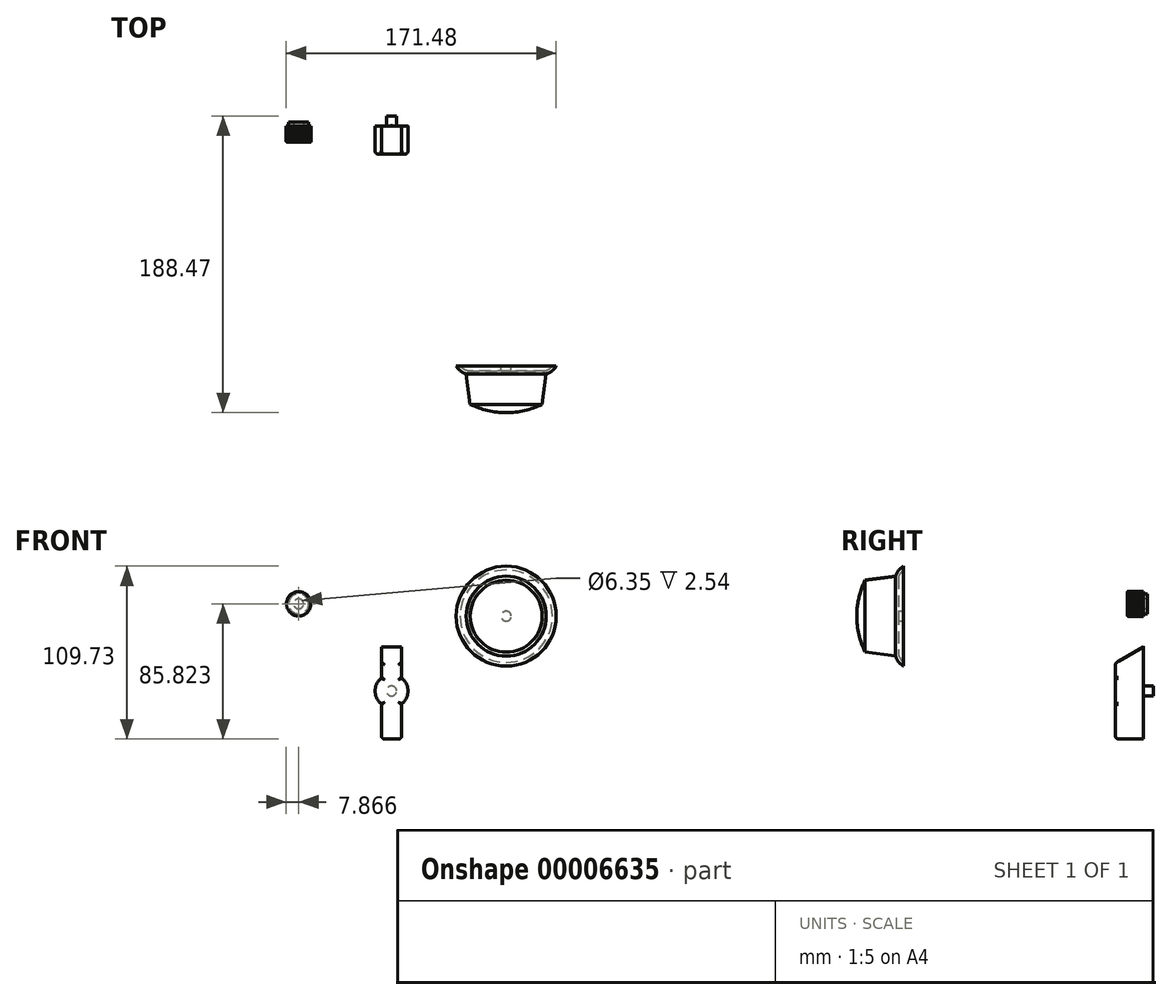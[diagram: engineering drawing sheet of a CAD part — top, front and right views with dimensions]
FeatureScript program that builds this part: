
annotation { "Feature Type Name" : "Feature", "Feature Type Description" : "" }
export const myFeature = defineFeature(function(context is Context, id is Id, definition is map)
    precondition{}
    {
        {
            var Q0;
            Q0=qCreatedBy(makeId("Front.planeOp"),FACE);
            var sketch = newSketch(context, id + "F0", { "sketchPlane" : qUnion([Q0])});
            skArc(sketch, "E0", {"start": v(-6.35, 8.25) * mm, "mid": v(-10.41, 0) * mm, "end": v(-6.35, -8.25) * mm});
            skLineSegment(sketch, "E1", {"start": v(0, 61) * mm, "end": v(0, -89) * mm, "construction": true});
            skLineSegment(sketch, "E2", {"start": v(-6.35, 27.94) * mm, "end": v(-6.35, 8.25) * mm});
            skLineSegment(sketch, "E3", {"start": v(-6.35, -30.48) * mm, "end": v(6.35, -30.48) * mm});
            skLineSegment(sketch, "E4", {"start": v(6.35, -30.48) * mm, "end": v(6.35, -8.25) * mm});
            skLineSegment(sketch, "E5", {"start": v(6.35, 27.94) * mm, "end": v(-6.35, 27.94) * mm});
            skPoint(sketch, "E6", {"position": v(0, 27.94) * mm});
            skLineSegment(sketch, "E7.trimOffspring", {"start": v(6.35, 8.25) * mm, "end": v(6.35, 27.94) * mm});
            skLineSegment(sketch, "E8.trimOffspring", {"start": v(-6.35, -8.25) * mm, "end": v(-6.35, -30.48) * mm});
            skArc(sketch, "E9.trimOffspring", {"start": v(6.35, -8.25) * mm, "mid": v(10.41, 0) * mm, "end": v(6.35, 8.25) * mm});
            skCircle(sketch, "E10", {"center": v(0, 0) * mm, "radius": 3.18 * mm});
            skSolve(sketch);
        }
        {
            var Q0;
            Q0=makeQuery(id+"F0.imprint","IMPRINT",FACE,{"disambiguationData":[TD([[makeQuery(id+"F0.imprint","IMPRINT",EDGE,{"derivedFrom":sQuery(id+"F0.wireOp",EDGE,"E0")}),1.0]])]});
            var Q1;
            Q1=makeQuery(id+"F0.imprint","IMPRINT",FACE,{"disambiguationData":[TD([[makeQuery(id+"F0.imprint","IMPRINT",EDGE,{"derivedFrom":sQuery(id+"F0.wireOp",EDGE,"E10")}),1.0]])]});
            extrude(context, id + "F1", {"entities" : qUnion([Q0, Q1]), "depth" : 17.78 * mm});
        }
        {
            var Q0;
            Q0=makeQuery(id+"F0.imprint","IMPRINT",FACE,{"disambiguationData":[TD([[makeQuery(id+"F0.imprint","IMPRINT",EDGE,{"derivedFrom":sQuery(id+"F0.wireOp",EDGE,"E10")}),1.0]])]});
            var Q1;
            Q1=sQuery(id+"F0.wireOp",EDGE,"E10");
            extrude(context, id + "F2", {"entities" : qUnion([Q0]), "operationType" : NewBodyOperationType.ADD, "surfaceEntities" : qUnion([Q1]), "oppositeDirection" : true, "depth" : 6.35 * mm});
        }
        {
            var Q0;
            Q0=makeQuery(id+"F1.opExtrude","SWEPT_FACE",FACE,{"disambiguationData":[OSD([sQuery(id+"F0.wireOp",EDGE,"E2")])]});
            var sketch = newSketch(context, id + "F3", { "sketchPlane" : qUnion([Q0])});
            skLineSegment(sketch, "E11", {"start": v(-11.17, 0) * mm, "end": v(28.92, 0) * mm, "construction": true});
            skLineSegment(sketch, "E12", {"start": v(0, 27.94) * mm, "end": v(17.78, 17.78) * mm});
            skLineSegment(sketch, "E13", {"start": v(0, 27.94) * mm, "end": v(17.78, 27.94) * mm});
            skLineSegment(sketch, "E14", {"start": v(17.78, 27.94) * mm, "end": v(17.78, 17.78) * mm});
            skSolve(sketch);
        }
        {
            var Q0;
            Q0=makeQuery(id+"F3.imprint","IMPRINT",FACE,{"disambiguationData":[TD([[makeQuery(id+"F3.imprint","IMPRINT",EDGE,{"derivedFrom":sQuery(id+"F3.wireOp",EDGE,"E12")}),1.0]])]});
            extrude(context, id + "F4", {"entities" : qUnion([Q0]), "operationType" : NewBodyOperationType.REMOVE, "oppositeDirection" : true, "depth" : 12.7 * mm});
        }
        {
            var Q0;
            Q0=makeQuery(id+"F4.boolean.opBoolean","COPY",FACE,{"derivedFrom":makeQuery(id+"F4.opExtrude","SWEPT_FACE",FACE,{"disambiguationData":[OSD([sQuery(id+"F3.wireOp",EDGE,"E12")])]})});
            var sketch = newSketch(context, id + "F5", { "sketchPlane" : qUnion([Q0])});
            skLineSegment(sketch, "E15", {"start": v(-0.64, 13.86) * mm, "end": v(0.64, 13.86) * mm});
            skLineSegment(sketch, "E16", {"start": v(0.63, 13.86) * mm, "end": v(0.64, -6.62) * mm});
            skLineSegment(sketch, "E17", {"start": v(0.63, -6.62) * mm, "end": v(-0.63, -6.62) * mm});
            skLineSegment(sketch, "E18", {"start": v(-0.63, -6.62) * mm, "end": v(-0.64, 13.86) * mm});
            skSolve(sketch);
        }
        {
            var Q0;
            Q0 = qSketchRegion(id + "F5", true);
            extrude(context, id + "F6", {"entities" : qUnion([Q0]), "operationType" : NewBodyOperationType.REMOVE, "oppositeDirection" : true, "depth" : 0.25 * mm});
        }
        {
            var Q0;
            Q0=makeQuery(id+"F1.opExtrude","CAP_FACE",FACE,{"disambiguationData":[OSD([sQuery(id+"F0.wireOp",EDGE,"E0"),sQuery(id+"F0.wireOp",EDGE,"E2"),sQuery(id+"F0.wireOp",EDGE,"E3"),sQuery(id+"F0.wireOp",EDGE,"E4"),sQuery(id+"F0.wireOp",EDGE,"E5"),sQuery(id+"F0.wireOp",EDGE,"E7.trimOffspring"),sQuery(id+"F0.wireOp",EDGE,"E8.trimOffspring"),sQuery(id+"F0.wireOp",EDGE,"E9.trimOffspring")])],"isStart":false});
            var sketch = newSketch(context, id + "F7", { "sketchPlane" : qUnion([Q0])});
            skLineSegment(sketch, "E19", {"start": v(-0.64, 17.78) * mm, "end": v(-0.64, 0) * mm});
            skLineSegment(sketch, "E20", {"start": v(-0.64, 17.78) * mm, "end": v(0.63, 17.78) * mm});
            skLineSegment(sketch, "E21", {"start": v(0.63, 17.78) * mm, "end": v(0.63, 0) * mm});
            skLineSegment(sketch, "E22", {"start": v(-0.64, 0) * mm, "end": v(0.63, 0) * mm});
            skSolve(sketch);
        }
        {
            var Q0;
            Q0=makeQuery(id+"F7.imprint","IMPRINT",FACE,{"disambiguationData":[TD([[makeQuery(id+"F7.imprint","IMPRINT",EDGE,{"derivedFrom":sQuery(id+"F7.wireOp",EDGE,"E19")}),1.0]])]});
            extrude(context, id + "F8", {"entities" : qUnion([Q0]), "operationType" : NewBodyOperationType.REMOVE, "oppositeDirection" : true, "depth" : 0.25 * mm});
        }
        {
            var Q0;
            {var subQ0=sQuery(id+"F0.wireOp",EDGE,"E2");Q0=makeQuery(id+"F6.boolean.opBoolean","SPLIT",FACE,{"disambiguationData":[TD([makeQuery(id+"F1.opExtrude","SWEPT_FACE",FACE,{"disambiguationData":[OSD([subQ0])]})])],"derivedFrom":makeQuery(id+"F4.boolean.opBoolean","COPY",FACE,{"derivedFrom":makeQuery(id+"F4.opExtrude","SWEPT_FACE",FACE,{"disambiguationData":[OSD([sQuery(id+"F3.wireOp",EDGE,"E12")])]})})});}
            var sketch = newSketch(context, id + "F9", { "sketchPlane" : qUnion([Q0])});
            skLineSegment(sketch, "E23", {"start": v(-0.64, 13.86) * mm, "end": v(-0.63, -6.62) * mm});
            skLineSegment(sketch, "E24", {"start": v(-0.63, -6.62) * mm, "end": v(0.67, -6.62) * mm});
            skLineSegment(sketch, "E25", {"start": v(0.67, -6.62) * mm, "end": v(0.67, 13.86) * mm});
            skLineSegment(sketch, "E26", {"start": v(0.67, 13.86) * mm, "end": v(-0.64, 13.86) * mm});
            skSolve(sketch);
        }
        {
            var Q0;
            Q0=makeQuery(id+"F9.imprint","IMPRINT",FACE,{"disambiguationData":[TD([[makeQuery(id+"F9.imprint","IMPRINT",EDGE,{"derivedFrom":sQuery(id+"F9.wireOp",EDGE,"E23")}),-1.0]])]});
            extrude(context, id + "F10", {"entities" : qUnion([Q0]), "oppositeDirection" : true, "depth" : 0.25 * mm});
        }
        {
            var Q0;
            Q0=makeQuery(id+"F1.opExtrude","CAP_FACE",FACE,{"disambiguationData":[OSD([sQuery(id+"F0.wireOp",EDGE,"E0"),sQuery(id+"F0.wireOp",EDGE,"E2"),sQuery(id+"F0.wireOp",EDGE,"E3"),sQuery(id+"F0.wireOp",EDGE,"E4"),sQuery(id+"F0.wireOp",EDGE,"E5"),sQuery(id+"F0.wireOp",EDGE,"E7.trimOffspring"),sQuery(id+"F0.wireOp",EDGE,"E8.trimOffspring"),sQuery(id+"F0.wireOp",EDGE,"E9.trimOffspring")])],"isStart":false});
            var sketch = newSketch(context, id + "F11", { "sketchPlane" : qUnion([Q0])});
            skLineSegment(sketch, "E27", {"start": v(-0.64, 17.78) * mm, "end": v(-0.64, 0) * mm});
            skLineSegment(sketch, "E28", {"start": v(-0.64, 0) * mm, "end": v(0.63, 0) * mm});
            skLineSegment(sketch, "E29", {"start": v(0.63, 0) * mm, "end": v(0.63, 17.78) * mm});
            skLineSegment(sketch, "E30", {"start": v(0.63, 17.78) * mm, "end": v(-0.64, 17.78) * mm});
            skSolve(sketch);
        }
        {
            var Q0;
            Q0=makeQuery(id+"F11.imprint","IMPRINT",FACE,{"disambiguationData":[TD([[makeQuery(id+"F11.imprint","IMPRINT",EDGE,{"derivedFrom":sQuery(id+"F11.wireOp",EDGE,"E27")}),1.0]])]});
            extrude(context, id + "F12", {"entities" : qUnion([Q0]), "operationType" : NewBodyOperationType.ADD, "oppositeDirection" : true, "depth" : 0.25 * mm});
        }
        {
            var Q0;
            Q0=makeQuery(id+"F1.opExtrude","SWEPT_EDGE",EDGE,{"disambiguationData":[OSD([sQuery(id+"F0.wireOp",EDGE,"E3"),sQuery(id+"F0.wireOp",EDGE,"E8.trimOffspring")])]});
            var Q1;
            Q1=makeQuery(id+"F1.opExtrude","SWEPT_EDGE",EDGE,{"disambiguationData":[OSD([sQuery(id+"F0.wireOp",EDGE,"E3"),sQuery(id+"F0.wireOp",EDGE,"E4")])]});
            var Q2;
            Q2=makeQuery(id+"F1.opExtrude","CAP_EDGE",EDGE,{"disambiguationData":[OSD([sQuery(id+"F0.wireOp",EDGE,"E4")])],"isStart":false});
            var Q3;
            Q3=makeQuery(id+"F1.opExtrude","CAP_EDGE",EDGE,{"disambiguationData":[OSD([sQuery(id+"F0.wireOp",EDGE,"E9.trimOffspring")])],"isStart":false});
            var Q4;
            Q4=makeQuery(id+"F1.opExtrude","CAP_EDGE",EDGE,{"disambiguationData":[OSD([sQuery(id+"F0.wireOp",EDGE,"E7.trimOffspring")])],"isStart":false});
            var Q5;
            Q5=makeQuery(id+"F4.boolean.opBoolean","COPY",EDGE,{"derivedFrom":makeQuery(id+"F4.opExtrude","CAP_EDGE",EDGE,{"disambiguationData":[OSD([sQuery(id+"F3.wireOp",EDGE,"E12")])],"isStart":false})});
            var Q6;
            {var subQ0=sQuery(id+"F0.wireOp",EDGE,"E2");var subQ1=sQuery(id+"F3.wireOp",EDGE,"E12");var subQ2=sQuery(id+"F0.wireOp",EDGE,"E7.trimOffspring");Q6=makeQuery(id+"F6.boolean.opBoolean","SPLIT",EDGE,{"disambiguationData":[TD([makeQuery(id+"F1.opExtrude","SWEPT_FACE",FACE,{"disambiguationData":[OSD([subQ2])]})])],"derivedFrom":makeQuery(id+"F4.boolean.opBoolean","COPY",EDGE,{"derivedFrom":makeQuery(id+"F4.opExtrude","SWEPT_EDGE",EDGE,{"disambiguationData":[OSD([subQ0,subQ1,sQuery(id+"F3.wireOp",EDGE,"E14")])]})})});}
            var Q7;
            {var subQ0=sQuery(id+"F0.wireOp",EDGE,"E2");var subQ1=sQuery(id+"F3.wireOp",EDGE,"E12");Q7=makeQuery(id+"F6.boolean.opBoolean","SPLIT",EDGE,{"disambiguationData":[TD([makeQuery(id+"F1.opExtrude","SWEPT_FACE",FACE,{"disambiguationData":[OSD([subQ0])]})])],"derivedFrom":makeQuery(id+"F4.boolean.opBoolean","COPY",EDGE,{"derivedFrom":makeQuery(id+"F4.opExtrude","SWEPT_EDGE",EDGE,{"disambiguationData":[OSD([subQ0,subQ1,sQuery(id+"F3.wireOp",EDGE,"E14")])]})})});}
            var Q8;
            Q8=makeQuery(id+"F12.boolean.opBoolean","MERGE",EDGE,{"derivedFrom":[makeQuery(id+"F10.opExtrude","CAP_EDGE",EDGE,{"disambiguationData":[OSD([sQuery(id+"F9.wireOp",EDGE,"E24")])],"isStart":true}),makeQuery(id+"F12.opExtrude","CAP_EDGE",EDGE,{"disambiguationData":[OSD([sQuery(id+"F11.wireOp",EDGE,"E30")])],"isStart":true})]});
            var Q9;
            Q9=makeQuery(id+"F4.boolean.opBoolean","COPY",EDGE,{"derivedFrom":makeQuery(id+"F4.opExtrude","CAP_EDGE",EDGE,{"disambiguationData":[OSD([sQuery(id+"F3.wireOp",EDGE,"E12")])],"isStart":true})});
            var Q10;
            Q10=makeQuery(id+"F1.opExtrude","CAP_EDGE",EDGE,{"disambiguationData":[OSD([sQuery(id+"F0.wireOp",EDGE,"E2")])],"isStart":false});
            var Q11;
            Q11=makeQuery(id+"F1.opExtrude","CAP_EDGE",EDGE,{"disambiguationData":[OSD([sQuery(id+"F0.wireOp",EDGE,"E0")])],"isStart":false});
            var Q12;
            Q12=makeQuery(id+"F1.opExtrude","CAP_EDGE",EDGE,{"disambiguationData":[OSD([sQuery(id+"F0.wireOp",EDGE,"E3")])],"isStart":false});
            var Q13;
            Q13=makeQuery(id+"F1.opExtrude","CAP_EDGE",EDGE,{"disambiguationData":[OSD([sQuery(id+"F0.wireOp",EDGE,"E8.trimOffspring")])],"isStart":false});
            fillet(context, id + "F13", {"entities" : qUnion([Q0, Q1, Q2, Q3, Q4, Q5, Q6, Q7, Q8, Q9, Q10, Q11, Q12, Q13]), "radius" : 1.78 * mm, "tangentPropagation" : true, "allowEdgeOverflow" : false});
        }
        {
            var Q0;
            Q0=makeQuery(id+"F1.opExtrude","SWEPT_EDGE",EDGE,{"disambiguationData":[OSD([sQuery(id+"F0.wireOp",EDGE,"E0"),sQuery(id+"F0.wireOp",EDGE,"E2")])]});
            var Q1;
            Q1=makeQuery(id+"F1.opExtrude","SWEPT_EDGE",EDGE,{"disambiguationData":[OSD([sQuery(id+"F0.wireOp",EDGE,"E0"),sQuery(id+"F0.wireOp",EDGE,"E8.trimOffspring")])]});
            var Q2;
            Q2=makeQuery(id+"F1.opExtrude","SWEPT_EDGE",EDGE,{"disambiguationData":[OSD([sQuery(id+"F0.wireOp",EDGE,"E7.trimOffspring"),sQuery(id+"F0.wireOp",EDGE,"E9.trimOffspring")])]});
            var Q3;
            Q3=makeQuery(id+"F1.opExtrude","SWEPT_EDGE",EDGE,{"disambiguationData":[OSD([sQuery(id+"F0.wireOp",EDGE,"E4"),sQuery(id+"F0.wireOp",EDGE,"E9.trimOffspring")])]});
            fillet(context, id + "F14", {"entities" : qUnion([Q0, Q1, Q2, Q3]), "radius" : 0.76 * mm, "tangentPropagation" : true, "allowEdgeOverflow" : false});
        }
        {
            var Q0;
            Q0=qCreatedBy(makeId("Front.planeOp"),FACE);
            var sketch = newSketch(context, id + "F15", { "sketchPlane" : qUnion([Q0])});
            skLineSegment(sketch, "E31", {"start": v(-59.01, 70.18) * mm, "end": v(-59.01, 47.47) * mm, "construction": true});
            skLineSegment(sketch, "E32", {"start": v(-78.46, 55.34) * mm, "end": v(-35.07, 55.34) * mm, "construction": true});
            skCircle(sketch, "E33", {"center": v(-59.01, 55.34) * mm, "radius": 3.18 * mm});
            skCircle(sketch, "E34", {"center": v(-59.01, 55.34) * mm, "radius": 7.62 * mm});
            skLineSegment(sketch, "E35", {"start": v(-59.01, 55.34) * mm, "end": v(-57.52, 65.95) * mm, "construction": true});
            skLineSegment(sketch, "E36", {"start": v(-59.01, 63.22) * mm, "end": v(-58.48, 62.94) * mm});
            skLineSegment(sketch, "E37", {"start": v(-58.48, 62.94) * mm, "end": v(-57.92, 63.14) * mm});
            skLineSegment(sketch, "E38.1.0", {"start": v(-60.11, 63.14) * mm, "end": v(-59.55, 62.94) * mm});
            skLineSegment(sketch, "E38.1.1", {"start": v(-59.55, 62.94) * mm, "end": v(-59.01, 63.22) * mm});
            skLineSegment(sketch, "E38.2.0", {"start": v(-61.18, 62.91) * mm, "end": v(-60.6, 62.8) * mm});
            skLineSegment(sketch, "E38.2.1", {"start": v(-60.6, 62.8) * mm, "end": v(-60.11, 63.14) * mm});
            skLineSegment(sketch, "E38.3.0", {"start": v(-62.22, 62.54) * mm, "end": v(-61.62, 62.5) * mm});
            skLineSegment(sketch, "E38.3.1", {"start": v(-61.62, 62.5) * mm, "end": v(-61.18, 62.91) * mm});
            skLineSegment(sketch, "E38.4.0", {"start": v(-63.19, 62.02) * mm, "end": v(-62.6, 62.07) * mm});
            skLineSegment(sketch, "E38.4.1", {"start": v(-62.6, 62.07) * mm, "end": v(-62.22, 62.54) * mm});
            skLineSegment(sketch, "E38.5.0", {"start": v(-64.08, 61.37) * mm, "end": v(-63.5, 61.5) * mm});
            skLineSegment(sketch, "E38.5.1", {"start": v(-63.5, 61.5) * mm, "end": v(-63.19, 62.02) * mm});
            skLineSegment(sketch, "E38.6.0", {"start": v(-64.87, 60.61) * mm, "end": v(-64.3, 60.82) * mm});
            skLineSegment(sketch, "E38.6.1", {"start": v(-64.3, 60.82) * mm, "end": v(-64.08, 61.37) * mm});
            skLineSegment(sketch, "E38.7.0", {"start": v(-65.54, 59.75) * mm, "end": v(-65.02, 60.03) * mm});
            skLineSegment(sketch, "E38.7.1", {"start": v(-65.02, 60.03) * mm, "end": v(-64.87, 60.61) * mm});
            skLineSegment(sketch, "E38.8.0", {"start": v(-66.1, 58.8) * mm, "end": v(-65.61, 59.15) * mm});
            skLineSegment(sketch, "E38.8.1", {"start": v(-65.61, 59.15) * mm, "end": v(-65.54, 59.75) * mm});
            skLineSegment(sketch, "E38.9.0", {"start": v(-66.5, 57.78) * mm, "end": v(-66.08, 58.2) * mm});
            skLineSegment(sketch, "E38.9.1", {"start": v(-66.08, 58.2) * mm, "end": v(-66.1, 58.8) * mm});
            skLineSegment(sketch, "E38.10.0", {"start": v(-66.77, 56.71) * mm, "end": v(-66.4, 57.19) * mm});
            skLineSegment(sketch, "E38.10.1", {"start": v(-66.4, 57.19) * mm, "end": v(-66.5, 57.78) * mm});
            skLineSegment(sketch, "E38.11.0", {"start": v(-66.88, 55.62) * mm, "end": v(-66.6, 56.14) * mm});
            skLineSegment(sketch, "E38.11.1", {"start": v(-66.6, 56.14) * mm, "end": v(-66.77, 56.71) * mm});
            skLineSegment(sketch, "E38.12.0", {"start": v(-66.85, 54.52) * mm, "end": v(-66.63, 55.08) * mm});
            skLineSegment(sketch, "E38.12.1", {"start": v(-66.63, 55.08) * mm, "end": v(-66.88, 55.62) * mm});
            skLineSegment(sketch, "E38.13.0", {"start": v(-66.65, 53.44) * mm, "end": v(-66.52, 54.02) * mm});
            skLineSegment(sketch, "E38.13.1", {"start": v(-66.52, 54.02) * mm, "end": v(-66.85, 54.52) * mm});
            skLineSegment(sketch, "E38.14.0", {"start": v(-66.31, 52.4) * mm, "end": v(-66.26, 52.99) * mm});
            skLineSegment(sketch, "E38.14.1", {"start": v(-66.26, 52.99) * mm, "end": v(-66.65, 53.44) * mm});
            skLineSegment(sketch, "E38.15.0", {"start": v(-65.83, 51.4) * mm, "end": v(-65.86, 52) * mm});
            skLineSegment(sketch, "E38.15.1", {"start": v(-65.86, 52) * mm, "end": v(-66.31, 52.4) * mm});
            skLineSegment(sketch, "E38.16.0", {"start": v(-65.22, 50.5) * mm, "end": v(-65.33, 51.08) * mm});
            skLineSegment(sketch, "E38.16.1", {"start": v(-65.33, 51.08) * mm, "end": v(-65.83, 51.4) * mm});
            skLineSegment(sketch, "E38.17.0", {"start": v(-64.48, 49.68) * mm, "end": v(-64.68, 50.24) * mm});
            skLineSegment(sketch, "E38.17.1", {"start": v(-64.68, 50.24) * mm, "end": v(-65.22, 50.5) * mm});
            skLineSegment(sketch, "E38.18.0", {"start": v(-63.64, 48.97) * mm, "end": v(-63.91, 49.5) * mm});
            skLineSegment(sketch, "E38.18.1", {"start": v(-63.91, 49.5) * mm, "end": v(-64.48, 49.68) * mm});
            skLineSegment(sketch, "E38.19.0", {"start": v(-62.71, 48.4) * mm, "end": v(-63.05, 48.88) * mm});
            skLineSegment(sketch, "E38.19.1", {"start": v(-63.05, 48.88) * mm, "end": v(-63.64, 48.97) * mm});
            skLineSegment(sketch, "E38.20.0", {"start": v(-61.7, 47.94) * mm, "end": v(-62.11, 48.38) * mm});
            skLineSegment(sketch, "E38.20.1", {"start": v(-62.11, 48.38) * mm, "end": v(-62.71, 48.4) * mm});
            skLineSegment(sketch, "E38.21.0", {"start": v(-60.65, 47.64) * mm, "end": v(-61.11, 48.02) * mm});
            skLineSegment(sketch, "E38.21.1", {"start": v(-61.11, 48.02) * mm, "end": v(-61.7, 47.94) * mm});
            skLineSegment(sketch, "E38.22.0", {"start": v(-59.56, 47.49) * mm, "end": v(-60.07, 47.8) * mm});
            skLineSegment(sketch, "E38.22.1", {"start": v(-60.07, 47.8) * mm, "end": v(-60.65, 47.64) * mm});
            skLineSegment(sketch, "E38.23.0", {"start": v(-58.46, 47.49) * mm, "end": v(-59.01, 47.72) * mm});
            skLineSegment(sketch, "E38.23.1", {"start": v(-59.01, 47.72) * mm, "end": v(-59.56, 47.49) * mm});
            skLineSegment(sketch, "E38.24.0", {"start": v(-57.38, 47.64) * mm, "end": v(-57.95, 47.8) * mm});
            skLineSegment(sketch, "E38.24.1", {"start": v(-57.95, 47.8) * mm, "end": v(-58.46, 47.49) * mm});
            skLineSegment(sketch, "E38.25.0", {"start": v(-56.32, 47.94) * mm, "end": v(-56.91, 48.02) * mm});
            skLineSegment(sketch, "E38.25.1", {"start": v(-56.91, 48.02) * mm, "end": v(-57.38, 47.64) * mm});
            skLineSegment(sketch, "E38.26.0", {"start": v(-55.32, 48.4) * mm, "end": v(-55.91, 48.38) * mm});
            skLineSegment(sketch, "E38.26.1", {"start": v(-55.91, 48.38) * mm, "end": v(-56.32, 47.94) * mm});
            skLineSegment(sketch, "E38.27.0", {"start": v(-54.39, 48.97) * mm, "end": v(-54.98, 48.88) * mm});
            skLineSegment(sketch, "E38.27.1", {"start": v(-54.98, 48.88) * mm, "end": v(-55.32, 48.4) * mm});
            skLineSegment(sketch, "E38.28.0", {"start": v(-53.54, 49.68) * mm, "end": v(-54.12, 49.5) * mm});
            skLineSegment(sketch, "E38.28.1", {"start": v(-54.12, 49.5) * mm, "end": v(-54.39, 48.97) * mm});
            skLineSegment(sketch, "E38.29.0", {"start": v(-52.8, 50.5) * mm, "end": v(-53.35, 50.24) * mm});
            skLineSegment(sketch, "E38.29.1", {"start": v(-53.35, 50.24) * mm, "end": v(-53.54, 49.68) * mm});
            skLineSegment(sketch, "E38.30.0", {"start": v(-52.2, 51.4) * mm, "end": v(-52.7, 51.08) * mm});
            skLineSegment(sketch, "E38.30.1", {"start": v(-52.7, 51.08) * mm, "end": v(-52.8, 50.5) * mm});
            skLineSegment(sketch, "E38.31.0", {"start": v(-51.71, 52.4) * mm, "end": v(-52.17, 52) * mm});
            skLineSegment(sketch, "E38.31.1", {"start": v(-52.17, 52) * mm, "end": v(-52.2, 51.4) * mm});
            skLineSegment(sketch, "E38.32.0", {"start": v(-51.37, 53.44) * mm, "end": v(-51.77, 52.99) * mm});
            skLineSegment(sketch, "E38.32.1", {"start": v(-51.77, 52.99) * mm, "end": v(-51.71, 52.4) * mm});
            skLineSegment(sketch, "E38.33.0", {"start": v(-51.18, 54.52) * mm, "end": v(-51.5, 54.02) * mm});
            skLineSegment(sketch, "E38.33.1", {"start": v(-51.5, 54.02) * mm, "end": v(-51.37, 53.44) * mm});
            skLineSegment(sketch, "E38.34.0", {"start": v(-51.14, 55.62) * mm, "end": v(-51.4, 55.08) * mm});
            skLineSegment(sketch, "E38.34.1", {"start": v(-51.4, 55.08) * mm, "end": v(-51.18, 54.52) * mm});
            skLineSegment(sketch, "E38.35.0", {"start": v(-51.26, 56.71) * mm, "end": v(-51.44, 56.14) * mm});
            skLineSegment(sketch, "E38.35.1", {"start": v(-51.44, 56.14) * mm, "end": v(-51.14, 55.62) * mm});
            skLineSegment(sketch, "E38.36.0", {"start": v(-51.53, 57.78) * mm, "end": v(-51.62, 57.19) * mm});
            skLineSegment(sketch, "E38.36.1", {"start": v(-51.62, 57.19) * mm, "end": v(-51.26, 56.71) * mm});
            skLineSegment(sketch, "E38.37.0", {"start": v(-51.94, 58.8) * mm, "end": v(-51.95, 58.2) * mm});
            skLineSegment(sketch, "E38.37.1", {"start": v(-51.95, 58.2) * mm, "end": v(-51.53, 57.78) * mm});
            skLineSegment(sketch, "E38.38.0", {"start": v(-52.49, 59.75) * mm, "end": v(-52.42, 59.15) * mm});
            skLineSegment(sketch, "E38.38.1", {"start": v(-52.42, 59.15) * mm, "end": v(-51.94, 58.8) * mm});
            skLineSegment(sketch, "E38.39.0", {"start": v(-53.16, 60.61) * mm, "end": v(-53, 60.03) * mm});
            skLineSegment(sketch, "E38.39.1", {"start": v(-53, 60.03) * mm, "end": v(-52.49, 59.75) * mm});
            skLineSegment(sketch, "E38.40.0", {"start": v(-53.95, 61.37) * mm, "end": v(-53.72, 60.82) * mm});
            skLineSegment(sketch, "E38.40.1", {"start": v(-53.72, 60.82) * mm, "end": v(-53.16, 60.61) * mm});
            skLineSegment(sketch, "E38.41.0", {"start": v(-54.84, 62.02) * mm, "end": v(-54.54, 61.5) * mm});
            skLineSegment(sketch, "E38.41.1", {"start": v(-54.54, 61.5) * mm, "end": v(-53.95, 61.37) * mm});
            skLineSegment(sketch, "E38.42.0", {"start": v(-55.81, 62.54) * mm, "end": v(-55.44, 62.07) * mm});
            skLineSegment(sketch, "E38.42.1", {"start": v(-55.44, 62.07) * mm, "end": v(-54.84, 62.02) * mm});
            skLineSegment(sketch, "E38.43.0", {"start": v(-56.84, 62.91) * mm, "end": v(-56.4, 62.5) * mm});
            skLineSegment(sketch, "E38.43.1", {"start": v(-56.4, 62.5) * mm, "end": v(-55.81, 62.54) * mm});
            skLineSegment(sketch, "E38.44.0", {"start": v(-57.92, 63.14) * mm, "end": v(-57.43, 62.8) * mm});
            skLineSegment(sketch, "E38.44.1", {"start": v(-57.43, 62.8) * mm, "end": v(-56.84, 62.91) * mm});
            skCircle(sketch, "E39", {"center": v(-59.01, 55.34) * mm, "radius": 6.35 * mm});
            skSolve(sketch);
        }
        {
            var Q0;
            {var subQ0=sQuery(id+"F15.wireOp",EDGE,"E38.22.0");Q0=makeQuery(id+"F15.imprint","IMPRINT",FACE,{"disambiguationData":[TD([[makeQuery(id+"F15.imprint","IMPRINT",EDGE,{"derivedFrom":subQ0}),-1.0]])]});}
            var Q1;
            {var subQ1=sQuery(id+"F15.wireOp",EDGE,"E38.6.0");Q1=makeQuery(id+"F15.imprint","IMPRINT",FACE,{"disambiguationData":[TD([[makeQuery(id+"F15.imprint","IMPRINT",EDGE,{"derivedFrom":subQ1}),-1.0]])]});}
            var Q2;
            {var subQ1=sQuery(id+"F15.wireOp",EDGE,"E38.29.0");Q2=makeQuery(id+"F15.imprint","IMPRINT",FACE,{"disambiguationData":[TD([[makeQuery(id+"F15.imprint","IMPRINT",EDGE,{"derivedFrom":subQ1}),-1.0]])]});}
            var Q3;
            {var subQ1=sQuery(id+"F15.wireOp",EDGE,"E38.13.0");Q3=makeQuery(id+"F15.imprint","IMPRINT",FACE,{"disambiguationData":[TD([[makeQuery(id+"F15.imprint","IMPRINT",EDGE,{"derivedFrom":subQ1}),-1.0]])]});}
            var Q4;
            {var subQ1=sQuery(id+"F15.wireOp",EDGE,"E38.7.0");Q4=makeQuery(id+"F15.imprint","IMPRINT",FACE,{"disambiguationData":[TD([[makeQuery(id+"F15.imprint","IMPRINT",EDGE,{"derivedFrom":subQ1}),-1.0]])]});}
            var Q5;
            {var subQ1=sQuery(id+"F15.wireOp",EDGE,"E38.30.0");Q5=makeQuery(id+"F15.imprint","IMPRINT",FACE,{"disambiguationData":[TD([[makeQuery(id+"F15.imprint","IMPRINT",EDGE,{"derivedFrom":subQ1}),-1.0]])]});}
            var Q6;
            {var subQ1=sQuery(id+"F15.wireOp",EDGE,"E38.21.0");Q6=makeQuery(id+"F15.imprint","IMPRINT",FACE,{"disambiguationData":[TD([[makeQuery(id+"F15.imprint","IMPRINT",EDGE,{"derivedFrom":subQ1}),-1.0]])]});}
            var Q7;
            {var subQ1=sQuery(id+"F15.wireOp",EDGE,"E38.5.0");Q7=makeQuery(id+"F15.imprint","IMPRINT",FACE,{"disambiguationData":[TD([[makeQuery(id+"F15.imprint","IMPRINT",EDGE,{"derivedFrom":subQ1}),-1.0]])]});}
            var Q8;
            Q8=makeQuery(id+"F15.imprint","IMPRINT",FACE,{"disambiguationData":[TD([[makeQuery(id+"F15.imprint","IMPRINT",EDGE,{"derivedFrom":sQuery(id+"F15.wireOp",EDGE,"E33")}),-1.0]])]});
            var Q9;
            {var subQ1=sQuery(id+"F15.wireOp",EDGE,"E38.19.0");Q9=makeQuery(id+"F15.imprint","IMPRINT",FACE,{"disambiguationData":[TD([[makeQuery(id+"F15.imprint","IMPRINT",EDGE,{"derivedFrom":subQ1}),-1.0]])]});}
            var Q10;
            {var subQ1=sQuery(id+"F15.wireOp",EDGE,"E38.3.0");Q10=makeQuery(id+"F15.imprint","IMPRINT",FACE,{"disambiguationData":[TD([[makeQuery(id+"F15.imprint","IMPRINT",EDGE,{"derivedFrom":subQ1}),-1.0]])]});}
            var Q11;
            {var subQ1=sQuery(id+"F15.wireOp",EDGE,"E38.26.0");Q11=makeQuery(id+"F15.imprint","IMPRINT",FACE,{"disambiguationData":[TD([[makeQuery(id+"F15.imprint","IMPRINT",EDGE,{"derivedFrom":subQ1}),-1.0]])]});}
            var Q12;
            {var subQ1=sQuery(id+"F15.wireOp",EDGE,"E38.10.0");Q12=makeQuery(id+"F15.imprint","IMPRINT",FACE,{"disambiguationData":[TD([[makeQuery(id+"F15.imprint","IMPRINT",EDGE,{"derivedFrom":subQ1}),-1.0]])]});}
            var Q13;
            {var subQ1=sQuery(id+"F15.wireOp",EDGE,"E38.17.0");Q13=makeQuery(id+"F15.imprint","IMPRINT",FACE,{"disambiguationData":[TD([[makeQuery(id+"F15.imprint","IMPRINT",EDGE,{"derivedFrom":subQ1}),-1.0]])]});}
            var Q14;
            {var subQ1=sQuery(id+"F15.wireOp",EDGE,"E38.43.0");Q14=makeQuery(id+"F15.imprint","IMPRINT",FACE,{"disambiguationData":[TD([[makeQuery(id+"F15.imprint","IMPRINT",EDGE,{"derivedFrom":subQ1}),-1.0]])]});}
            var Q15;
            {var subQ1=sQuery(id+"F15.wireOp",EDGE,"E38.41.0");Q15=makeQuery(id+"F15.imprint","IMPRINT",FACE,{"disambiguationData":[TD([[makeQuery(id+"F15.imprint","IMPRINT",EDGE,{"derivedFrom":subQ1}),-1.0]])]});}
            var Q16;
            {var subQ1=sQuery(id+"F15.wireOp",EDGE,"E38.40.0");Q16=makeQuery(id+"F15.imprint","IMPRINT",FACE,{"disambiguationData":[TD([[makeQuery(id+"F15.imprint","IMPRINT",EDGE,{"derivedFrom":subQ1}),-1.0]])]});}
            var Q17;
            {var subQ1=sQuery(id+"F15.wireOp",EDGE,"E38.37.0");Q17=makeQuery(id+"F15.imprint","IMPRINT",FACE,{"disambiguationData":[TD([[makeQuery(id+"F15.imprint","IMPRINT",EDGE,{"derivedFrom":subQ1}),-1.0]])]});}
            var Q18;
            {var subQ1=sQuery(id+"F15.wireOp",EDGE,"E38.36.0");Q18=makeQuery(id+"F15.imprint","IMPRINT",FACE,{"disambiguationData":[TD([[makeQuery(id+"F15.imprint","IMPRINT",EDGE,{"derivedFrom":subQ1}),-1.0]])]});}
            var Q19;
            {var subQ1=sQuery(id+"F15.wireOp",EDGE,"E38.35.0");Q19=makeQuery(id+"F15.imprint","IMPRINT",FACE,{"disambiguationData":[TD([[makeQuery(id+"F15.imprint","IMPRINT",EDGE,{"derivedFrom":subQ1}),-1.0]])]});}
            var Q20;
            Q20=makeQuery(id+"F15.imprint","IMPRINT",FACE,{"disambiguationData":[TD([[makeQuery(id+"F15.imprint","IMPRINT",EDGE,{"derivedFrom":sQuery(id+"F15.wireOp",EDGE,"E33")}),1.0]])]});
            var Q21;
            Q21=makeQuery(id+"F15.imprint","IMPRINT",FACE,{"disambiguationData":[TD([[makeQuery(id+"F15.imprint","IMPRINT",EDGE,{"derivedFrom":sQuery(id+"F15.wireOp",EDGE,"E39")}),-1.0]])]});
            var Q22;
            {var subQ1=sQuery(id+"F15.wireOp",EDGE,"E38.24.0");Q22=makeQuery(id+"F15.imprint","IMPRINT",FACE,{"disambiguationData":[TD([[makeQuery(id+"F15.imprint","IMPRINT",EDGE,{"derivedFrom":subQ1}),-1.0]])]});}
            var Q23;
            {var subQ1=sQuery(id+"F15.wireOp",EDGE,"E38.8.0");Q23=makeQuery(id+"F15.imprint","IMPRINT",FACE,{"disambiguationData":[TD([[makeQuery(id+"F15.imprint","IMPRINT",EDGE,{"derivedFrom":subQ1}),-1.0]])]});}
            var Q24;
            {var subQ1=sQuery(id+"F15.wireOp",EDGE,"E38.18.0");Q24=makeQuery(id+"F15.imprint","IMPRINT",FACE,{"disambiguationData":[TD([[makeQuery(id+"F15.imprint","IMPRINT",EDGE,{"derivedFrom":subQ1}),-1.0]])]});}
            var Q25;
            {var subQ1=sQuery(id+"F15.wireOp",EDGE,"E38.15.0");Q25=makeQuery(id+"F15.imprint","IMPRINT",FACE,{"disambiguationData":[TD([[makeQuery(id+"F15.imprint","IMPRINT",EDGE,{"derivedFrom":subQ1}),-1.0]])]});}
            var Q26;
            {var subQ1=sQuery(id+"F15.wireOp",EDGE,"E38.31.0");Q26=makeQuery(id+"F15.imprint","IMPRINT",FACE,{"disambiguationData":[TD([[makeQuery(id+"F15.imprint","IMPRINT",EDGE,{"derivedFrom":subQ1}),-1.0]])]});}
            var Q27;
            {var subQ1=sQuery(id+"F15.wireOp",EDGE,"E38.23.0");Q27=makeQuery(id+"F15.imprint","IMPRINT",FACE,{"disambiguationData":[TD([[makeQuery(id+"F15.imprint","IMPRINT",EDGE,{"derivedFrom":subQ1}),-1.0]])]});}
            var Q28;
            {var subQ1=sQuery(id+"F15.wireOp",EDGE,"E38.14.0");Q28=makeQuery(id+"F15.imprint","IMPRINT",FACE,{"disambiguationData":[TD([[makeQuery(id+"F15.imprint","IMPRINT",EDGE,{"derivedFrom":subQ1}),-1.0]])]});}
            var Q29;
            {var subQ1=sQuery(id+"F15.wireOp",EDGE,"E38.27.0");Q29=makeQuery(id+"F15.imprint","IMPRINT",FACE,{"disambiguationData":[TD([[makeQuery(id+"F15.imprint","IMPRINT",EDGE,{"derivedFrom":subQ1}),-1.0]])]});}
            var Q30;
            {var subQ1=sQuery(id+"F15.wireOp",EDGE,"E38.11.0");Q30=makeQuery(id+"F15.imprint","IMPRINT",FACE,{"disambiguationData":[TD([[makeQuery(id+"F15.imprint","IMPRINT",EDGE,{"derivedFrom":subQ1}),-1.0]])]});}
            var Q31;
            {var subQ1=sQuery(id+"F15.wireOp",EDGE,"E38.12.0");Q31=makeQuery(id+"F15.imprint","IMPRINT",FACE,{"disambiguationData":[TD([[makeQuery(id+"F15.imprint","IMPRINT",EDGE,{"derivedFrom":subQ1}),-1.0]])]});}
            var Q32;
            {var subQ1=sQuery(id+"F15.wireOp",EDGE,"E38.28.0");Q32=makeQuery(id+"F15.imprint","IMPRINT",FACE,{"disambiguationData":[TD([[makeQuery(id+"F15.imprint","IMPRINT",EDGE,{"derivedFrom":subQ1}),-1.0]])]});}
            var Q33;
            {var subQ1=sQuery(id+"F15.wireOp",EDGE,"E38.2.0");Q33=makeQuery(id+"F15.imprint","IMPRINT",FACE,{"disambiguationData":[TD([[makeQuery(id+"F15.imprint","IMPRINT",EDGE,{"derivedFrom":subQ1}),-1.0]])]});}
            var Q34;
            {var subQ1=sQuery(id+"F15.wireOp",EDGE,"E38.9.0");Q34=makeQuery(id+"F15.imprint","IMPRINT",FACE,{"disambiguationData":[TD([[makeQuery(id+"F15.imprint","IMPRINT",EDGE,{"derivedFrom":subQ1}),-1.0]])]});}
            var Q35;
            {var subQ1=sQuery(id+"F15.wireOp",EDGE,"E38.4.0");Q35=makeQuery(id+"F15.imprint","IMPRINT",FACE,{"disambiguationData":[TD([[makeQuery(id+"F15.imprint","IMPRINT",EDGE,{"derivedFrom":subQ1}),-1.0]])]});}
            var Q36;
            {var subQ1=sQuery(id+"F15.wireOp",EDGE,"E38.1.0");Q36=makeQuery(id+"F15.imprint","IMPRINT",FACE,{"disambiguationData":[TD([[makeQuery(id+"F15.imprint","IMPRINT",EDGE,{"derivedFrom":subQ1}),-1.0]])]});}
            var Q37;
            {var subQ1=sQuery(id+"F15.wireOp",EDGE,"E36");Q37=makeQuery(id+"F15.imprint","IMPRINT",FACE,{"disambiguationData":[TD([[makeQuery(id+"F15.imprint","IMPRINT",EDGE,{"derivedFrom":subQ1}),-1.0]])]});}
            var Q38;
            {var subQ1=sQuery(id+"F15.wireOp",EDGE,"E38.33.0");Q38=makeQuery(id+"F15.imprint","IMPRINT",FACE,{"disambiguationData":[TD([[makeQuery(id+"F15.imprint","IMPRINT",EDGE,{"derivedFrom":subQ1}),-1.0]])]});}
            var Q39;
            {var subQ1=sQuery(id+"F15.wireOp",EDGE,"E37");Q39=makeQuery(id+"F15.imprint","IMPRINT",FACE,{"disambiguationData":[TD([[makeQuery(id+"F15.imprint","IMPRINT",EDGE,{"derivedFrom":subQ1}),-1.0]])]});}
            var Q40;
            {var subQ1=sQuery(id+"F15.wireOp",EDGE,"E38.42.0");Q40=makeQuery(id+"F15.imprint","IMPRINT",FACE,{"disambiguationData":[TD([[makeQuery(id+"F15.imprint","IMPRINT",EDGE,{"derivedFrom":subQ1}),-1.0]])]});}
            var Q41;
            {var subQ1=sQuery(id+"F15.wireOp",EDGE,"E38.39.0");Q41=makeQuery(id+"F15.imprint","IMPRINT",FACE,{"disambiguationData":[TD([[makeQuery(id+"F15.imprint","IMPRINT",EDGE,{"derivedFrom":subQ1}),-1.0]])]});}
            var Q42;
            {var subQ1=sQuery(id+"F15.wireOp",EDGE,"E38.38.0");Q42=makeQuery(id+"F15.imprint","IMPRINT",FACE,{"disambiguationData":[TD([[makeQuery(id+"F15.imprint","IMPRINT",EDGE,{"derivedFrom":subQ1}),-1.0]])]});}
            var Q43;
            {var subQ1=sQuery(id+"F15.wireOp",EDGE,"E38.25.0");Q43=makeQuery(id+"F15.imprint","IMPRINT",FACE,{"disambiguationData":[TD([[makeQuery(id+"F15.imprint","IMPRINT",EDGE,{"derivedFrom":subQ1}),-1.0]])]});}
            var Q44;
            {var subQ1=sQuery(id+"F15.wireOp",EDGE,"E38.16.0");Q44=makeQuery(id+"F15.imprint","IMPRINT",FACE,{"disambiguationData":[TD([[makeQuery(id+"F15.imprint","IMPRINT",EDGE,{"derivedFrom":subQ1}),-1.0]])]});}
            var Q45;
            {var subQ1=sQuery(id+"F15.wireOp",EDGE,"E38.32.0");Q45=makeQuery(id+"F15.imprint","IMPRINT",FACE,{"disambiguationData":[TD([[makeQuery(id+"F15.imprint","IMPRINT",EDGE,{"derivedFrom":subQ1}),-1.0]])]});}
            var Q46;
            {var subQ1=sQuery(id+"F15.wireOp",EDGE,"E38.20.0");Q46=makeQuery(id+"F15.imprint","IMPRINT",FACE,{"disambiguationData":[TD([[makeQuery(id+"F15.imprint","IMPRINT",EDGE,{"derivedFrom":subQ1}),-1.0]])]});}
            var Q47;
            {var subQ1=sQuery(id+"F15.wireOp",EDGE,"E38.34.0");Q47=makeQuery(id+"F15.imprint","IMPRINT",FACE,{"disambiguationData":[TD([[makeQuery(id+"F15.imprint","IMPRINT",EDGE,{"derivedFrom":subQ1}),-1.0]])]});}
            extrude(context, id + "F16", {"entities" : qUnion([Q0, Q1, Q2, Q3, Q4, Q5, Q6, Q7, Q8, Q9, Q10, Q11, Q12, Q13, Q14, Q15, Q16, Q17, Q18, Q19, Q20, Q21, Q22, Q23, Q24, Q25, Q26, Q27, Q28, Q29, Q30, Q31, Q32, Q33, Q34, Q35, Q36, Q37, Q38, Q39, Q40, Q41, Q42, Q43, Q44, Q45, Q46, Q47]), "depth" : 10.16 * mm});
        }
        {
            var Q0;
            Q0=makeQuery(id+"F15.imprint","IMPRINT",FACE,{"disambiguationData":[TD([[makeQuery(id+"F15.imprint","IMPRINT",EDGE,{"derivedFrom":sQuery(id+"F15.wireOp",EDGE,"E33")}),-1.0]])]});
            extrude(context, id + "F17", {"entities" : qUnion([Q0]), "operationType" : NewBodyOperationType.ADD, "oppositeDirection" : true, "depth" : 2.54 * mm});
        }
        {
            var Q0;
            Q0=makeQuery(id+"F16.opExtrude","CAP_EDGE",EDGE,{"disambiguationData":[OSD([sQuery(id+"F15.wireOp",EDGE,"E38.3.1")])],"isStart":false});
            var Q1;
            Q1=makeQuery(id+"F16.opExtrude","CAP_EDGE",EDGE,{"disambiguationData":[OSD([sQuery(id+"F15.wireOp",EDGE,"E38.2.0")])],"isStart":false});
            var Q2;
            Q2=makeQuery(id+"F16.opExtrude","CAP_EDGE",EDGE,{"disambiguationData":[OSD([sQuery(id+"F15.wireOp",EDGE,"E38.2.1")])],"isStart":false});
            var Q3;
            Q3=makeQuery(id+"F16.opExtrude","CAP_EDGE",EDGE,{"disambiguationData":[OSD([sQuery(id+"F15.wireOp",EDGE,"E38.1.0")])],"isStart":false});
            var Q4;
            Q4=makeQuery(id+"F16.opExtrude","CAP_EDGE",EDGE,{"disambiguationData":[OSD([sQuery(id+"F15.wireOp",EDGE,"E38.1.1")])],"isStart":false});
            var Q5;
            Q5=makeQuery(id+"F16.opExtrude","CAP_EDGE",EDGE,{"disambiguationData":[OSD([sQuery(id+"F15.wireOp",EDGE,"E36")])],"isStart":false});
            var Q6;
            Q6=makeQuery(id+"F16.opExtrude","CAP_EDGE",EDGE,{"disambiguationData":[OSD([sQuery(id+"F15.wireOp",EDGE,"E37")])],"isStart":false});
            var Q7;
            Q7=makeQuery(id+"F16.opExtrude","CAP_EDGE",EDGE,{"disambiguationData":[OSD([sQuery(id+"F15.wireOp",EDGE,"E38.44.0")])],"isStart":false});
            var Q8;
            Q8=makeQuery(id+"F16.opExtrude","CAP_EDGE",EDGE,{"disambiguationData":[OSD([sQuery(id+"F15.wireOp",EDGE,"E38.3.0")])],"isStart":false});
            var Q9;
            Q9=makeQuery(id+"F16.opExtrude","CAP_EDGE",EDGE,{"disambiguationData":[OSD([sQuery(id+"F15.wireOp",EDGE,"E38.4.1")])],"isStart":false});
            var Q10;
            Q10=makeQuery(id+"F16.opExtrude","CAP_EDGE",EDGE,{"disambiguationData":[OSD([sQuery(id+"F15.wireOp",EDGE,"E38.4.0")])],"isStart":false});
            var Q11;
            Q11=makeQuery(id+"F16.opExtrude","CAP_EDGE",EDGE,{"disambiguationData":[OSD([sQuery(id+"F15.wireOp",EDGE,"E38.5.1")])],"isStart":false});
            var Q12;
            Q12=makeQuery(id+"F16.opExtrude","CAP_EDGE",EDGE,{"disambiguationData":[OSD([sQuery(id+"F15.wireOp",EDGE,"E38.5.0")])],"isStart":false});
            var Q13;
            Q13=makeQuery(id+"F16.opExtrude","CAP_EDGE",EDGE,{"disambiguationData":[OSD([sQuery(id+"F15.wireOp",EDGE,"E38.6.1")])],"isStart":false});
            var Q14;
            Q14=makeQuery(id+"F16.opExtrude","CAP_EDGE",EDGE,{"disambiguationData":[OSD([sQuery(id+"F15.wireOp",EDGE,"E38.6.0")])],"isStart":false});
            var Q15;
            Q15=makeQuery(id+"F16.opExtrude","CAP_EDGE",EDGE,{"disambiguationData":[OSD([sQuery(id+"F15.wireOp",EDGE,"E38.44.1")])],"isStart":false});
            var Q16;
            Q16=makeQuery(id+"F16.opExtrude","CAP_EDGE",EDGE,{"disambiguationData":[OSD([sQuery(id+"F15.wireOp",EDGE,"E38.43.0")])],"isStart":false});
            var Q17;
            Q17=makeQuery(id+"F16.opExtrude","CAP_EDGE",EDGE,{"disambiguationData":[OSD([sQuery(id+"F15.wireOp",EDGE,"E38.43.1")])],"isStart":false});
            var Q18;
            Q18=makeQuery(id+"F16.opExtrude","CAP_EDGE",EDGE,{"disambiguationData":[OSD([sQuery(id+"F15.wireOp",EDGE,"E38.42.0")])],"isStart":false});
            var Q19;
            Q19=makeQuery(id+"F16.opExtrude","CAP_EDGE",EDGE,{"disambiguationData":[OSD([sQuery(id+"F15.wireOp",EDGE,"E38.42.1")])],"isStart":false});
            var Q20;
            Q20=makeQuery(id+"F16.opExtrude","CAP_EDGE",EDGE,{"disambiguationData":[OSD([sQuery(id+"F15.wireOp",EDGE,"E38.41.0")])],"isStart":false});
            var Q21;
            Q21=makeQuery(id+"F16.opExtrude","CAP_EDGE",EDGE,{"disambiguationData":[OSD([sQuery(id+"F15.wireOp",EDGE,"E38.41.1")])],"isStart":false});
            var Q22;
            Q22=makeQuery(id+"F16.opExtrude","CAP_EDGE",EDGE,{"disambiguationData":[OSD([sQuery(id+"F15.wireOp",EDGE,"E38.40.0")])],"isStart":false});
            var Q23;
            Q23=makeQuery(id+"F16.opExtrude","CAP_EDGE",EDGE,{"disambiguationData":[OSD([sQuery(id+"F15.wireOp",EDGE,"E38.40.1")])],"isStart":false});
            var Q24;
            Q24=makeQuery(id+"F16.opExtrude","CAP_EDGE",EDGE,{"disambiguationData":[OSD([sQuery(id+"F15.wireOp",EDGE,"E38.39.0")])],"isStart":false});
            var Q25;
            Q25=makeQuery(id+"F16.opExtrude","CAP_EDGE",EDGE,{"disambiguationData":[OSD([sQuery(id+"F15.wireOp",EDGE,"E38.39.1")])],"isStart":false});
            var Q26;
            Q26=makeQuery(id+"F16.opExtrude","CAP_EDGE",EDGE,{"disambiguationData":[OSD([sQuery(id+"F15.wireOp",EDGE,"E38.38.0")])],"isStart":false});
            var Q27;
            Q27=makeQuery(id+"F16.opExtrude","CAP_EDGE",EDGE,{"disambiguationData":[OSD([sQuery(id+"F15.wireOp",EDGE,"E38.38.1")])],"isStart":false});
            var Q28;
            Q28=makeQuery(id+"F16.opExtrude","CAP_FACE",FACE,{"disambiguationData":[OSD([sQuery(id+"F15.wireOp",EDGE,"E36"),sQuery(id+"F15.wireOp",EDGE,"E37"),sQuery(id+"F15.wireOp",EDGE,"E38.1.0"),sQuery(id+"F15.wireOp",EDGE,"E38.1.1"),sQuery(id+"F15.wireOp",EDGE,"E38.2.0"),sQuery(id+"F15.wireOp",EDGE,"E38.2.1"),sQuery(id+"F15.wireOp",EDGE,"E38.3.0"),sQuery(id+"F15.wireOp",EDGE,"E38.3.1"),sQuery(id+"F15.wireOp",EDGE,"E38.4.0"),sQuery(id+"F15.wireOp",EDGE,"E38.4.1"),sQuery(id+"F15.wireOp",EDGE,"E38.5.0"),sQuery(id+"F15.wireOp",EDGE,"E38.5.1"),sQuery(id+"F15.wireOp",EDGE,"E38.6.0"),sQuery(id+"F15.wireOp",EDGE,"E38.6.1"),sQuery(id+"F15.wireOp",EDGE,"E38.7.0"),sQuery(id+"F15.wireOp",EDGE,"E38.7.1"),sQuery(id+"F15.wireOp",EDGE,"E38.8.0"),sQuery(id+"F15.wireOp",EDGE,"E38.8.1"),sQuery(id+"F15.wireOp",EDGE,"E38.9.0"),sQuery(id+"F15.wireOp",EDGE,"E38.9.1"),sQuery(id+"F15.wireOp",EDGE,"E38.10.0"),sQuery(id+"F15.wireOp",EDGE,"E38.10.1"),sQuery(id+"F15.wireOp",EDGE,"E38.11.0"),sQuery(id+"F15.wireOp",EDGE,"E38.11.1"),sQuery(id+"F15.wireOp",EDGE,"E38.12.0"),sQuery(id+"F15.wireOp",EDGE,"E38.12.1"),sQuery(id+"F15.wireOp",EDGE,"E38.13.0"),sQuery(id+"F15.wireOp",EDGE,"E38.13.1"),sQuery(id+"F15.wireOp",EDGE,"E38.14.0"),sQuery(id+"F15.wireOp",EDGE,"E38.14.1"),sQuery(id+"F15.wireOp",EDGE,"E38.15.0"),sQuery(id+"F15.wireOp",EDGE,"E38.15.1"),sQuery(id+"F15.wireOp",EDGE,"E38.16.0"),sQuery(id+"F15.wireOp",EDGE,"E38.16.1"),sQuery(id+"F15.wireOp",EDGE,"E38.17.0"),sQuery(id+"F15.wireOp",EDGE,"E38.17.1"),sQuery(id+"F15.wireOp",EDGE,"E38.18.0"),sQuery(id+"F15.wireOp",EDGE,"E38.18.1"),sQuery(id+"F15.wireOp",EDGE,"E38.19.0"),sQuery(id+"F15.wireOp",EDGE,"E38.19.1"),sQuery(id+"F15.wireOp",EDGE,"E38.20.0"),sQuery(id+"F15.wireOp",EDGE,"E38.20.1"),sQuery(id+"F15.wireOp",EDGE,"E38.21.0"),sQuery(id+"F15.wireOp",EDGE,"E38.21.1"),sQuery(id+"F15.wireOp",EDGE,"E38.22.0"),sQuery(id+"F15.wireOp",EDGE,"E38.22.1"),sQuery(id+"F15.wireOp",EDGE,"E38.23.0"),sQuery(id+"F15.wireOp",EDGE,"E38.23.1"),sQuery(id+"F15.wireOp",EDGE,"E38.24.0"),sQuery(id+"F15.wireOp",EDGE,"E38.24.1"),sQuery(id+"F15.wireOp",EDGE,"E38.25.0"),sQuery(id+"F15.wireOp",EDGE,"E38.25.1"),sQuery(id+"F15.wireOp",EDGE,"E38.26.0"),sQuery(id+"F15.wireOp",EDGE,"E38.26.1"),sQuery(id+"F15.wireOp",EDGE,"E38.27.0"),sQuery(id+"F15.wireOp",EDGE,"E38.27.1"),sQuery(id+"F15.wireOp",EDGE,"E38.28.0"),sQuery(id+"F15.wireOp",EDGE,"E38.28.1"),sQuery(id+"F15.wireOp",EDGE,"E38.29.0"),sQuery(id+"F15.wireOp",EDGE,"E38.29.1"),sQuery(id+"F15.wireOp",EDGE,"E38.30.0"),sQuery(id+"F15.wireOp",EDGE,"E38.30.1"),sQuery(id+"F15.wireOp",EDGE,"E38.31.0"),sQuery(id+"F15.wireOp",EDGE,"E38.31.1"),sQuery(id+"F15.wireOp",EDGE,"E38.32.0"),sQuery(id+"F15.wireOp",EDGE,"E38.32.1"),sQuery(id+"F15.wireOp",EDGE,"E38.33.0"),sQuery(id+"F15.wireOp",EDGE,"E38.33.1"),sQuery(id+"F15.wireOp",EDGE,"E38.34.0"),sQuery(id+"F15.wireOp",EDGE,"E38.34.1"),sQuery(id+"F15.wireOp",EDGE,"E38.35.0"),sQuery(id+"F15.wireOp",EDGE,"E38.35.1"),sQuery(id+"F15.wireOp",EDGE,"E38.36.0"),sQuery(id+"F15.wireOp",EDGE,"E38.36.1"),sQuery(id+"F15.wireOp",EDGE,"E38.37.0"),sQuery(id+"F15.wireOp",EDGE,"E38.37.1"),sQuery(id+"F15.wireOp",EDGE,"E38.38.0"),sQuery(id+"F15.wireOp",EDGE,"E38.38.1"),sQuery(id+"F15.wireOp",EDGE,"E38.39.0"),sQuery(id+"F15.wireOp",EDGE,"E38.39.1"),sQuery(id+"F15.wireOp",EDGE,"E38.40.0"),sQuery(id+"F15.wireOp",EDGE,"E38.40.1"),sQuery(id+"F15.wireOp",EDGE,"E38.41.0"),sQuery(id+"F15.wireOp",EDGE,"E38.41.1"),sQuery(id+"F15.wireOp",EDGE,"E38.42.0"),sQuery(id+"F15.wireOp",EDGE,"E38.42.1"),sQuery(id+"F15.wireOp",EDGE,"E38.43.0"),sQuery(id+"F15.wireOp",EDGE,"E38.43.1"),sQuery(id+"F15.wireOp",EDGE,"E38.44.0"),sQuery(id+"F15.wireOp",EDGE,"E38.44.1")])],"isStart":false});
            var Q29;
            Q29=makeQuery(id+"F16.opExtrude","CAP_EDGE",EDGE,{"disambiguationData":[OSD([sQuery(id+"F15.wireOp",EDGE,"E38.37.0")])],"isStart":false});
            fillet(context, id + "F18", {"entities" : qUnion([Q0, Q1, Q2, Q3, Q4, Q5, Q6, Q7, Q8, Q9, Q10, Q11, Q12, Q13, Q14, Q15, Q16, Q17, Q18, Q19, Q20, Q21, Q22, Q23, Q24, Q25, Q26, Q27, Q28, Q29]), "radius" : 0.25 * mm, "tangentPropagation" : true, "allowEdgeOverflow" : false});
        }
        {
            var Q0;
            Q0=qCreatedBy(makeId("Front.planeOp"),FACE);
            cPlane(context, id + "F19", {"entities" : qUnion([Q0]), "cplaneType" : CPlaneType.OFFSET, "offset" : 152.4 * mm, "width" : 152.4 * mm, "height" : 152.4 * mm});
        }
        {
            var Q0;
            Q0=qCreatedBy(id+"F19.planeOp",FACE);
            var sketch = newSketch(context, id + "F20", { "sketchPlane" : qUnion([Q0])});
            skLineSegment(sketch, "E40", {"start": v(72.85, 87.69) * mm, "end": v(72.85, -6.98) * mm, "construction": true});
            skLineSegment(sketch, "E41", {"start": v(22.4, 47.5) * mm, "end": v(121.1, 47.5) * mm, "construction": true});
            skCircle(sketch, "E42", {"center": v(72.85, 47.5) * mm, "radius": 3.18 * mm});
            skCircle(sketch, "E43", {"center": v(72.85, 47.5) * mm, "radius": 22.86 * mm});
            skCircle(sketch, "E44", {"center": v(72.85, 47.5) * mm, "radius": 25.4 * mm});
            skCircle(sketch, "E45", {"center": v(72.85, 47.5) * mm, "radius": 31.75 * mm});
            skSolve(sketch);
        }
        {
            var Q0;
            Q0=qCreatedBy(makeId("Right.planeOp"),FACE);
            var Q1;
            Q1=sQuery(id+"F20.wireOp",VERTEX,"E45.center");
            cPlane(context, id + "F21", {"entities" : qUnion([Q0, Q1]), "cplaneType" : CPlaneType.PLANE_POINT, "offset" : 152.4 * mm, "width" : 152.4 * mm, "height" : 152.4 * mm});
        }
        {
            var Q0;
            Q0=qCreatedBy(id+"F21.planeOp",FACE);
            var sketch = newSketch(context, id + "F22", { "sketchPlane" : qUnion([Q0])});
            skLineSegment(sketch, "E46", {"start": v(-87.56, 47.5) * mm, "end": v(-224.72, 47.5) * mm, "construction": true});
            skLineSegment(sketch, "E47", {"start": v(-152.4, 50.67) * mm, "end": v(-155.54, 50.67) * mm});
            skLineSegment(sketch, "E48", {"start": v(-118.48, 79.25) * mm, "end": v(-170.34, 79.25) * mm, "construction": true});
            skLineSegment(sketch, "E49", {"start": v(-117.84, 72.9) * mm, "end": v(-179.37, 72.9) * mm, "construction": true});
            skLineSegment(sketch, "E50", {"start": v(-116.68, 70.36) * mm, "end": v(-188.05, 70.36) * mm, "construction": true});
            skLineSegment(sketch, "E51", {"start": v(-157.48, 82.41) * mm, "end": v(-157.48, 33.8) * mm, "construction": true});
            skLineSegment(sketch, "E52", {"start": v(-176.78, 83.34) * mm, "end": v(-176.78, 42.29) * mm, "construction": true});
            skLineSegment(sketch, "E53", {"start": v(-182.12, 83.58) * mm, "end": v(-182.12, 40.42) * mm, "construction": true});
            skLineSegment(sketch, "E54", {"start": v(-157.48, 72.9) * mm, "end": v(-176.78, 70.36) * mm});
            skLineSegment(sketch, "E55", {"start": v(-152.4, 83.37) * mm, "end": v(-152.4, 34.54) * mm, "construction": true});
            skArc(sketch, "E56", {"start": v(-152.4, 79.25) * mm, "mid": v(-155.54, 76.55) * mm, "end": v(-157.48, 72.9) * mm});
            skArc(sketch, "E57.0", {"start": v(-152.4, 76.8) * mm, "mid": v(-154.32, 74.8) * mm, "end": v(-155.54, 72.3) * mm});
            skLineSegment(sketch, "E58", {"start": v(-152.4, 79.25) * mm, "end": v(-152.4, 76.8) * mm});
            skLineSegment(sketch, "E59", {"start": v(-155.54, 72.3) * mm, "end": v(-155.54, 50.67) * mm});
            skPoint(sketch, "E60.orphan", {"position": v(-152.4, 50.67) * mm});
            skArc(sketch, "E61", {"start": v(-176.78, 70.36) * mm, "mid": v(-180.77, 59.24) * mm, "end": v(-182.12, 47.5) * mm});
            skLineSegment(sketch, "E62", {"start": v(-152.4, 50.67) * mm, "end": v(-152.4, 47.5) * mm});
            skLineSegment(sketch, "E63", {"start": v(-152.4, 47.5) * mm, "end": v(-182.12, 47.5) * mm});
            skLineSegment(sketch, "E64", {"start": v(-176.78, 70.36) * mm, "end": v(-178.72, 85.1) * mm, "construction": true});
            skLineSegment(sketch, "E65", {"start": v(-176.78, 70.36) * mm, "end": v(-190.8, 68.51) * mm, "construction": true});
            skSolve(sketch);
        }
        {
            var Q0;
            Q0=makeQuery(id+"F22.imprint","IMPRINT",FACE,{"disambiguationData":[TD([[makeQuery(id+"F22.imprint","IMPRINT",EDGE,{"derivedFrom":sQuery(id+"F22.wireOp",EDGE,"E47")}),1.0]])]});
            var Q1;
            Q1=sQuery(id+"F22.wireOp",EDGE,"E46");
            revolve(context, id + "F23", {"entities" : qUnion([Q0]), "axis" : qUnion([Q1]), "revolveType" : RevolveType.FULL});
        }
    });
